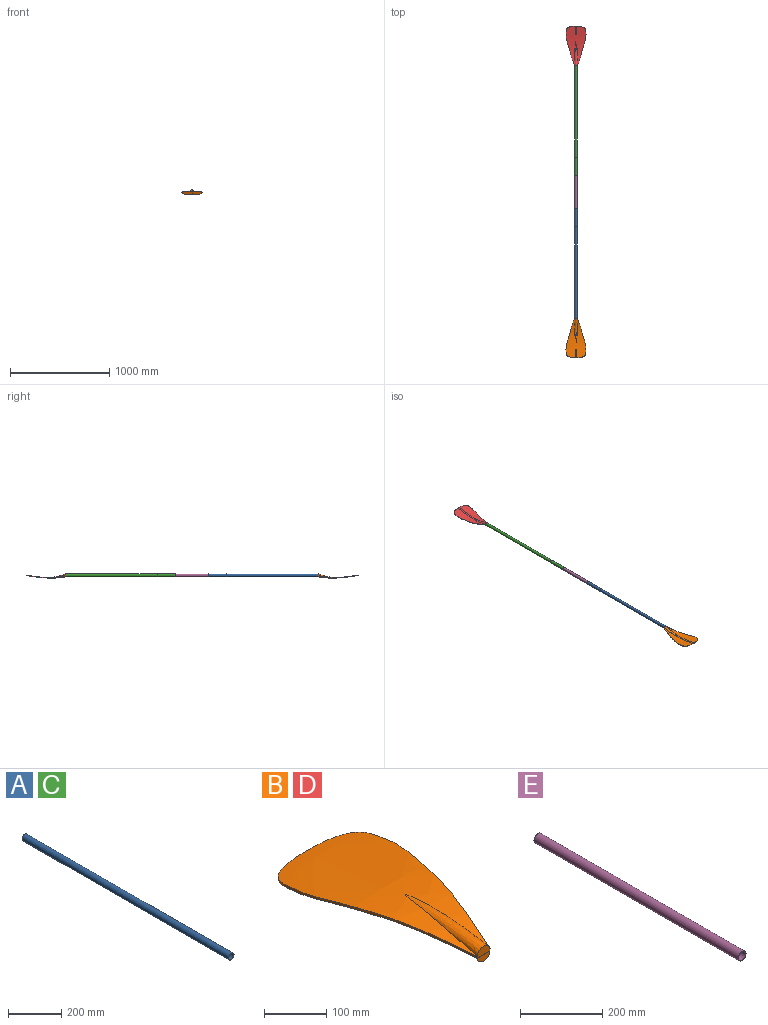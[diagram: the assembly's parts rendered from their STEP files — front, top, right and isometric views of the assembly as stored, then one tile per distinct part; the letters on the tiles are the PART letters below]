
ASSEMBLY  parts=5 mates=4
PART A: 4 faces, bbox 29x1100x29 mm
  f0: cylinder r=13.5mm len=1100mm, axis (0,1,0), area 93305.3mm2, adj f2,f3
  f1: cylinder r=14.5mm len=1100mm, axis (0,1,0), area 100216.8mm2, adj f2,f3
  f2: plane 29x29mm, normal (0,-1,0), area 88mm2, adj f0,f1
  f3: plane 29x29mm, normal (0,1,0), area 88mm2, adj f0,f1
PART B: 17 faces, bbox 204.5x403.8x65.8 mm
  f0: bspline ~400.79x99.76mm, area 1951.6mm2, adj f2,f6,f11,f12,f13
  f1: bspline ~400.79x99.77mm, area 1951.6mm2, adj f2,f5,f11,f12,f13
  f2: extruded ~400.31x201.44mm, area 51275mm2, adj f0,f1,f12,f13,f14
  f3: extruded ~0.48x0.16mm, area 0mm2, adj f9,f13,f16
  f4: plane 0.49x0.17mm, normal (0,0.24,-0.97), area 0.1mm2, adj f5,f10,f11,f13
  f5: plane 2.06x0.48mm, normal (1,0,0), area 0.5mm2, adj f1,f4,f13
  f6: plane 2.06x0.48mm, normal (-1,0,0), area 0.5mm2, adj f0,f7,f13
  f7: plane 0.49x0.17mm, normal (0,0.24,-0.97), area 0.1mm2, adj f6,f10,f11,f13
  f8: extruded ~0.48x0.16mm, area 0mm2, adj f9,f13,f16
  f9: plane 28.72x0.46mm, normal (0,0.24,-0.97), area 13.5mm2, adj f3,f8,f13,f16
  f10: bspline ~301.26x60.84mm, area 4388mm2, adj f4,f7,f11,f13,f15
  f11: extruded ~399.21x201.44mm, area 46593.8mm2, adj f0,f1,f4,f7,f10,f12,f15
  f12: plane 3.95x1.92mm, normal (0,0.99,-0.15), area 7.7mm2, adj f0,f1,f2,f11
  f13: plane 32.35x32.02mm, normal (0,-1,0), area 659.9mm2, adj f0,f1,f2,f3,f4,f5,f6,f7
  f14: bspline ~313.9x36.49mm, area 4390.1mm2, adj f2,f13
  f15: bspline ~349.84x65.6mm, area 5130.3mm2, adj f10,f11
  f16: bspline ~98.75x29.23mm, area 13.9mm2, adj f3,f8,f9,f13
PART C: same geometry as A
PART D: same geometry as B
PART E: 4 faces, bbox 27x700x27 mm
  f0: cylinder r=12.5mm len=700mm, axis (0,1,0), area 54977.9mm2, adj f2,f3
  f1: cylinder r=13.5mm len=700mm, axis (0,1,0), area 59376.1mm2, adj f2,f3
  f2: plane 27x27mm, normal (0,-1,0), area 81.7mm2, adj f0,f1
  f3: plane 27x27mm, normal (0,1,0), area 81.7mm2, adj f0,f1
PLACE A t=(0,-890,0)mm
PLACE B rot(axis=(-1,0,0),180deg) t=(0,-1440,0)mm
PLACE C rot(axis=(0,0,1),180deg) t=(0,550,0)mm
PLACE D rot(axis=(0,1,0),180deg) t=(0,1100,0)mm
PLACE E t=(0,-170,0)mm
MATE fastened B.f13 <-> A.f0  axis (0,1,0) through (0,-1440,0)mm
MATE slider C.f1 <-> E.f1  axis (0,-1,0) through (0,0,0)mm
MATE slider E.f0 <-> A.f1  axis (0,1,0) through (0,-520,0)mm
MATE fastened D.f13 <-> C.f0  axis (0,-1,0) through (0,1100,0)mm
